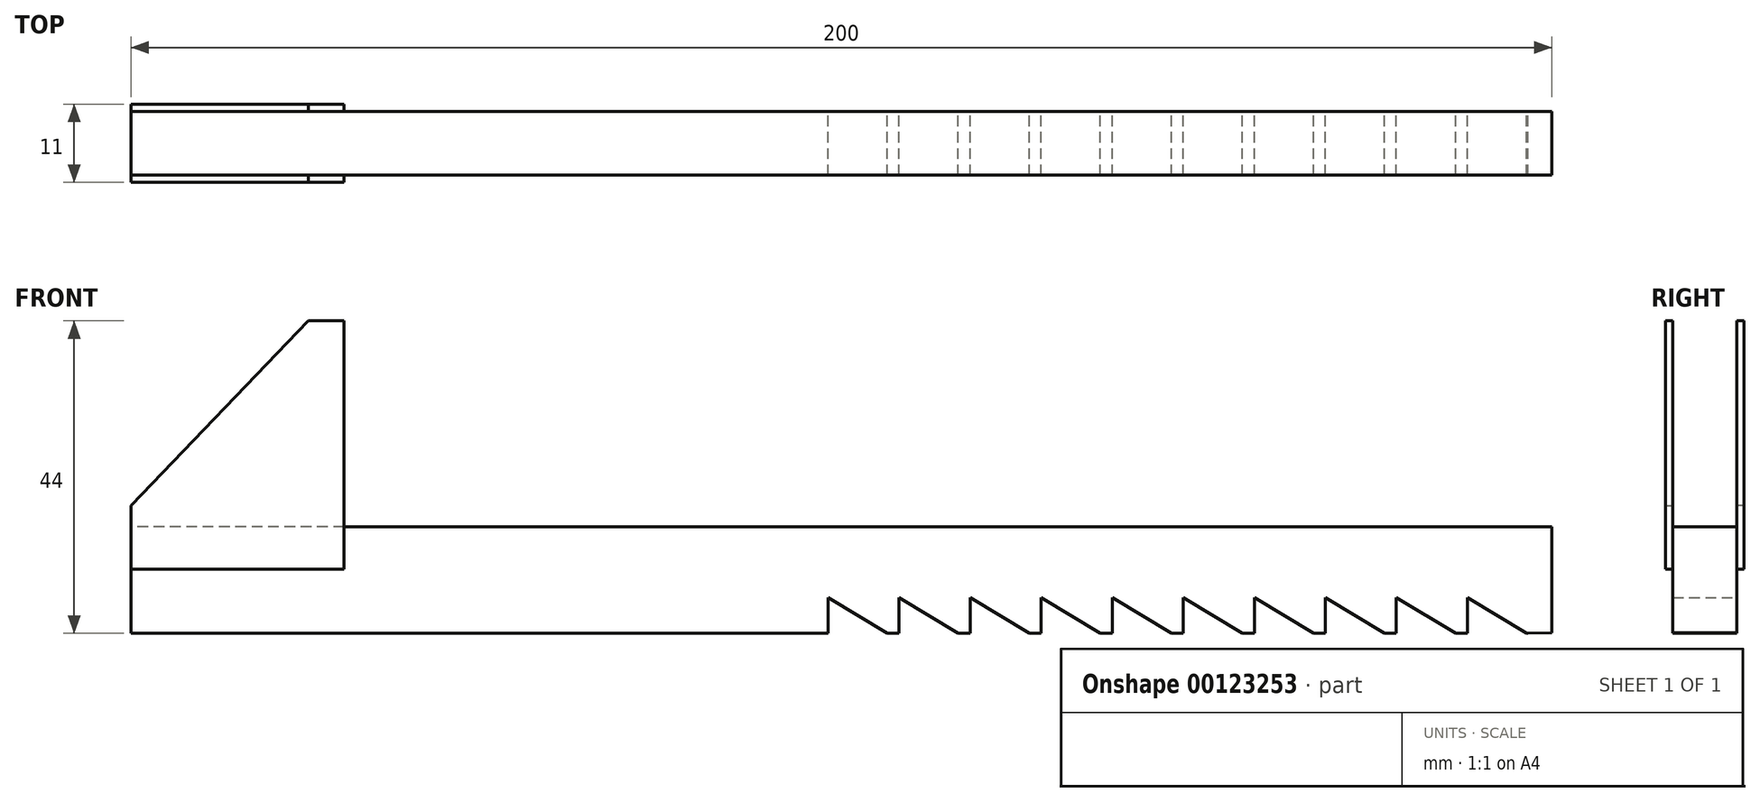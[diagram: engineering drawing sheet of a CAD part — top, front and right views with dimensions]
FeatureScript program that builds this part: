
annotation { "Feature Type Name" : "Feature", "Feature Type Description" : "" }
export const myFeature = defineFeature(function(context is Context, id is Id, definition is map)
    precondition{}
    {
        {
            var Q0;
            Q0=qCreatedBy(makeId("Front.planeOp"),FACE);
            var sketch = newSketch(context, id + "F0", { "sketchPlane" : qUnion([Q0])});
            skLineSegment(sketch, "E0", {"start": v(-7.13, 2.08) * mm, "end": v(-12, 5) * mm});
            skLineSegment(sketch, "E1", {"start": v(-12, 0) * mm, "end": v(-12, 5) * mm});
            skLineSegment(sketch, "E2", {"start": v(-3.67, 0) * mm, "end": v(-3.49, 0) * mm});
            skLineSegment(sketch, "E3.trimOffspring", {"start": v(-3.67, 0) * mm, "end": v(-10, 3.8) * mm});
            skPoint(sketch, "E4.start.orphan", {"position": v(0, 0) * mm});
            skPoint(sketch, "E5.orphan", {"position": v(-12, 0) * mm});
            skLineSegment(sketch, "E6.1.0.0", {"start": v(-2, 0) * mm, "end": v(-2, 5) * mm});
            skLineSegment(sketch, "E6.1.0.1", {"start": v(2.87, 2.08) * mm, "end": v(-2, 5) * mm});
            skLineSegment(sketch, "E6.1.0.2", {"start": v(6.33, 0) * mm, "end": v(0, 3.8) * mm});
            skLineSegment(sketch, "E6.1.0.3", {"start": v(6.33, 0) * mm, "end": v(6.51, 0) * mm});
            skLineSegment(sketch, "E6.2.0.0", {"start": v(8, 0) * mm, "end": v(8, 5) * mm});
            skLineSegment(sketch, "E6.2.0.1", {"start": v(12.87, 2.08) * mm, "end": v(8, 5) * mm});
            skLineSegment(sketch, "E6.2.0.2", {"start": v(16.33, 0) * mm, "end": v(10, 3.8) * mm});
            skLineSegment(sketch, "E6.2.0.3", {"start": v(16.33, 0) * mm, "end": v(16.51, 0) * mm});
            skLineSegment(sketch, "E6.3.0.0", {"start": v(18, 0) * mm, "end": v(18, 5) * mm});
            skLineSegment(sketch, "E6.3.0.1", {"start": v(22.87, 2.08) * mm, "end": v(18, 5) * mm});
            skLineSegment(sketch, "E6.3.0.2", {"start": v(26.33, 0) * mm, "end": v(20, 3.8) * mm});
            skLineSegment(sketch, "E6.3.0.3", {"start": v(26.33, 0) * mm, "end": v(26.51, 0) * mm});
            skLineSegment(sketch, "E6.4.0.0", {"start": v(28, 0) * mm, "end": v(28, 5) * mm});
            skLineSegment(sketch, "E6.4.0.1", {"start": v(32.87, 2.08) * mm, "end": v(28, 5) * mm});
            skLineSegment(sketch, "E6.4.0.2", {"start": v(36.33, 0) * mm, "end": v(30, 3.8) * mm});
            skLineSegment(sketch, "E6.4.0.3", {"start": v(36.33, 0) * mm, "end": v(36.51, 0) * mm});
            skLineSegment(sketch, "E6.5.0.0", {"start": v(38, 0) * mm, "end": v(38, 5) * mm});
            skLineSegment(sketch, "E6.5.0.1", {"start": v(42.87, 2.08) * mm, "end": v(38, 5) * mm});
            skLineSegment(sketch, "E6.5.0.2", {"start": v(46.33, 0) * mm, "end": v(40, 3.8) * mm});
            skLineSegment(sketch, "E6.5.0.3", {"start": v(46.33, 0) * mm, "end": v(46.51, 0) * mm});
            skLineSegment(sketch, "E6.6.0.0", {"start": v(48, 0) * mm, "end": v(48, 5) * mm});
            skLineSegment(sketch, "E6.6.0.1", {"start": v(52.87, 2.08) * mm, "end": v(48, 5) * mm});
            skLineSegment(sketch, "E6.6.0.2", {"start": v(56.33, 0) * mm, "end": v(50, 3.8) * mm});
            skLineSegment(sketch, "E6.6.0.3", {"start": v(56.33, 0) * mm, "end": v(56.51, 0) * mm});
            skLineSegment(sketch, "E6.7.0.0", {"start": v(58, 0) * mm, "end": v(58, 5) * mm});
            skLineSegment(sketch, "E6.7.0.1", {"start": v(62.87, 2.08) * mm, "end": v(58, 5) * mm});
            skLineSegment(sketch, "E6.7.0.2", {"start": v(66.33, 0) * mm, "end": v(60, 3.8) * mm});
            skLineSegment(sketch, "E6.7.0.3", {"start": v(66.33, 0) * mm, "end": v(66.51, 0) * mm});
            skLineSegment(sketch, "E6.8.0.0", {"start": v(68, 0) * mm, "end": v(68, 5) * mm});
            skLineSegment(sketch, "E6.8.0.1", {"start": v(72.87, 2.08) * mm, "end": v(68, 5) * mm});
            skLineSegment(sketch, "E6.8.0.2", {"start": v(76.33, 0) * mm, "end": v(70, 3.8) * mm});
            skLineSegment(sketch, "E6.8.0.3", {"start": v(76.33, 0) * mm, "end": v(76.51, 0) * mm});
            skLineSegment(sketch, "E6.9.0.0", {"start": v(78, 0) * mm, "end": v(78, 5) * mm});
            skLineSegment(sketch, "E6.9.0.1", {"start": v(82.87, 2.08) * mm, "end": v(78, 5) * mm});
            skLineSegment(sketch, "E6.9.0.2", {"start": v(86.33, 0) * mm, "end": v(80, 3.8) * mm});
            skLineSegment(sketch, "E6.9.0.3", {"start": v(86.33, 0) * mm, "end": v(86.51, 0) * mm});
            skLineSegment(sketch, "E6.direction1", {"start": v(-12, 0) * mm, "end": v(-2, 0) * mm, "construction": true});
            skLineSegment(sketch, "E7", {"start": v(89.9, 0.06) * mm, "end": v(89.9, 15) * mm});
            skLineSegment(sketch, "E8", {"start": v(89.9, 15) * mm, "end": v(-110.1, 15) * mm});
            skLineSegment(sketch, "E9", {"start": v(-110.1, 15) * mm, "end": v(-110.1, 0) * mm});
            skLineSegment(sketch, "E10", {"start": v(-12, 0) * mm, "end": v(-110.1, 0) * mm});
            skLineSegment(sketch, "E11", {"start": v(16.51, 0) * mm, "end": v(18, 0) * mm});
            skLineSegment(sketch, "E12", {"start": v(26.33, 0) * mm, "end": v(28, 0) * mm});
            skLineSegment(sketch, "E13", {"start": v(36.51, 0) * mm, "end": v(38, 0) * mm});
            skLineSegment(sketch, "E14", {"start": v(46.51, 0) * mm, "end": v(48, 0) * mm});
            skLineSegment(sketch, "E15", {"start": v(56.51, 0) * mm, "end": v(58, 0) * mm});
            skLineSegment(sketch, "E16", {"start": v(66.51, 0) * mm, "end": v(68, 0) * mm});
            skLineSegment(sketch, "E17", {"start": v(76.51, 0) * mm, "end": v(78, 0) * mm});
            skLineSegment(sketch, "E18", {"start": v(86.51, 0) * mm, "end": v(89.9, 0.06) * mm});
            skLineSegment(sketch, "E19", {"start": v(-3.49, 0) * mm, "end": v(-2, 0) * mm});
            skLineSegment(sketch, "E20", {"start": v(6.51, 0) * mm, "end": v(8, 0) * mm});
            skSolve(sketch);
        }
        {
            var Q0;
            Q0 = qSketchRegion(id + "F0", true);
            extrude(context, id + "F1", {"entities" : qUnion([Q0]), "endBound" : BoundingType.SYMMETRIC, "depth" : 9 * mm});
        }
        {
            var Q0;
            Q0=qCreatedBy(makeId("Front.planeOp"),FACE);
            cPlane(context, id + "F2", {"entities" : qUnion([Q0]), "cplaneType" : CPlaneType.OFFSET, "offset" : 4.5 * mm, "width" : 150 * mm, "height" : 150 * mm});
        }
        {
            var Q0;
            Q0=qCreatedBy(id+"F2.planeOp",FACE);
            var sketch = newSketch(context, id + "F3", { "sketchPlane" : qUnion([Q0])});
            skLineSegment(sketch, "E21", {"start": v(-85.1, 44) * mm, "end": v(-80.1, 44) * mm});
            skLineSegment(sketch, "E22", {"start": v(-80.1, 44) * mm, "end": v(-80.1, 9) * mm});
            skLineSegment(sketch, "E23", {"start": v(-80.1, 9) * mm, "end": v(-110.1, 9) * mm});
            skLineSegment(sketch, "E24", {"start": v(-110.1, 9) * mm, "end": v(-110.1, 18) * mm});
            skLineSegment(sketch, "E25", {"start": v(-110.1, 18) * mm, "end": v(-85.1, 44) * mm});
            skSolve(sketch);
        }
        {
            var Q0;
            Q0=makeQuery(id+"F3.imprint","IMPRINT",FACE,{"disambiguationData":[TD([[makeQuery(id+"F3.imprint","IMPRINT",EDGE,{"derivedFrom":sQuery(id+"F3.wireOp",EDGE,"E21")}),-1.0]])]});
            extrude(context, id + "F4", {"entities" : qUnion([Q0]), "operationType" : NewBodyOperationType.ADD, "depth" : 1 * mm});
        }
        {
            var Q0;
            Q0=makeQuery(id+"F1.opExtrude","SWEPT_BODY",BODY,{"disambiguationData":[OSD([sQuery(id+"F0.wireOp",EDGE,"E0"),sQuery(id+"F0.wireOp",EDGE,"E1"),sQuery(id+"F0.wireOp",EDGE,"E2"),sQuery(id+"F0.wireOp",EDGE,"E3.trimOffspring"),sQuery(id+"F0.wireOp",EDGE,"E6.1.0.0"),sQuery(id+"F0.wireOp",EDGE,"E6.1.0.1"),sQuery(id+"F0.wireOp",EDGE,"E6.1.0.2"),sQuery(id+"F0.wireOp",EDGE,"E6.1.0.3"),sQuery(id+"F0.wireOp",EDGE,"E6.2.0.0"),sQuery(id+"F0.wireOp",EDGE,"E6.2.0.1"),sQuery(id+"F0.wireOp",EDGE,"E6.2.0.2"),sQuery(id+"F0.wireOp",EDGE,"E6.2.0.3"),sQuery(id+"F0.wireOp",EDGE,"E6.3.0.0"),sQuery(id+"F0.wireOp",EDGE,"E6.3.0.1"),sQuery(id+"F0.wireOp",EDGE,"E6.3.0.2"),sQuery(id+"F0.wireOp",EDGE,"E6.4.0.0"),sQuery(id+"F0.wireOp",EDGE,"E6.4.0.1"),sQuery(id+"F0.wireOp",EDGE,"E6.4.0.2"),sQuery(id+"F0.wireOp",EDGE,"E6.4.0.3"),sQuery(id+"F0.wireOp",EDGE,"E6.5.0.0"),sQuery(id+"F0.wireOp",EDGE,"E6.5.0.1"),sQuery(id+"F0.wireOp",EDGE,"E6.5.0.2"),sQuery(id+"F0.wireOp",EDGE,"E6.5.0.3"),sQuery(id+"F0.wireOp",EDGE,"E6.6.0.0"),sQuery(id+"F0.wireOp",EDGE,"E6.6.0.1"),sQuery(id+"F0.wireOp",EDGE,"E6.6.0.2"),sQuery(id+"F0.wireOp",EDGE,"E6.6.0.3"),sQuery(id+"F0.wireOp",EDGE,"E6.7.0.0"),sQuery(id+"F0.wireOp",EDGE,"E6.7.0.1"),sQuery(id+"F0.wireOp",EDGE,"E6.7.0.2"),sQuery(id+"F0.wireOp",EDGE,"E6.7.0.3"),sQuery(id+"F0.wireOp",EDGE,"E6.8.0.0"),sQuery(id+"F0.wireOp",EDGE,"E6.8.0.1"),sQuery(id+"F0.wireOp",EDGE,"E6.8.0.2"),sQuery(id+"F0.wireOp",EDGE,"E6.8.0.3"),sQuery(id+"F0.wireOp",EDGE,"E6.9.0.0"),sQuery(id+"F0.wireOp",EDGE,"E6.9.0.1"),sQuery(id+"F0.wireOp",EDGE,"E6.9.0.2"),sQuery(id+"F0.wireOp",EDGE,"E6.9.0.3"),sQuery(id+"F0.wireOp",EDGE,"E7"),sQuery(id+"F0.wireOp",EDGE,"E8"),sQuery(id+"F0.wireOp",EDGE,"E9"),sQuery(id+"F0.wireOp",EDGE,"E10"),sQuery(id+"F0.wireOp",EDGE,"E11"),sQuery(id+"F0.wireOp",EDGE,"E12"),sQuery(id+"F0.wireOp",EDGE,"E13"),sQuery(id+"F0.wireOp",EDGE,"E14"),sQuery(id+"F0.wireOp",EDGE,"E15"),sQuery(id+"F0.wireOp",EDGE,"E16"),sQuery(id+"F0.wireOp",EDGE,"E17"),sQuery(id+"F0.wireOp",EDGE,"E18"),sQuery(id+"F0.wireOp",EDGE,"E19"),sQuery(id+"F0.wireOp",EDGE,"E20")])]});
            var Q1;
            Q1=qCreatedBy(makeId("Front.planeOp"),FACE);
            mirror(context, id + "F5", {"operationType" : NewBodyOperationType.ADD, "entities" : qUnion([Q0]), "mirrorPlane" : qUnion([Q1])});
        }
    });
